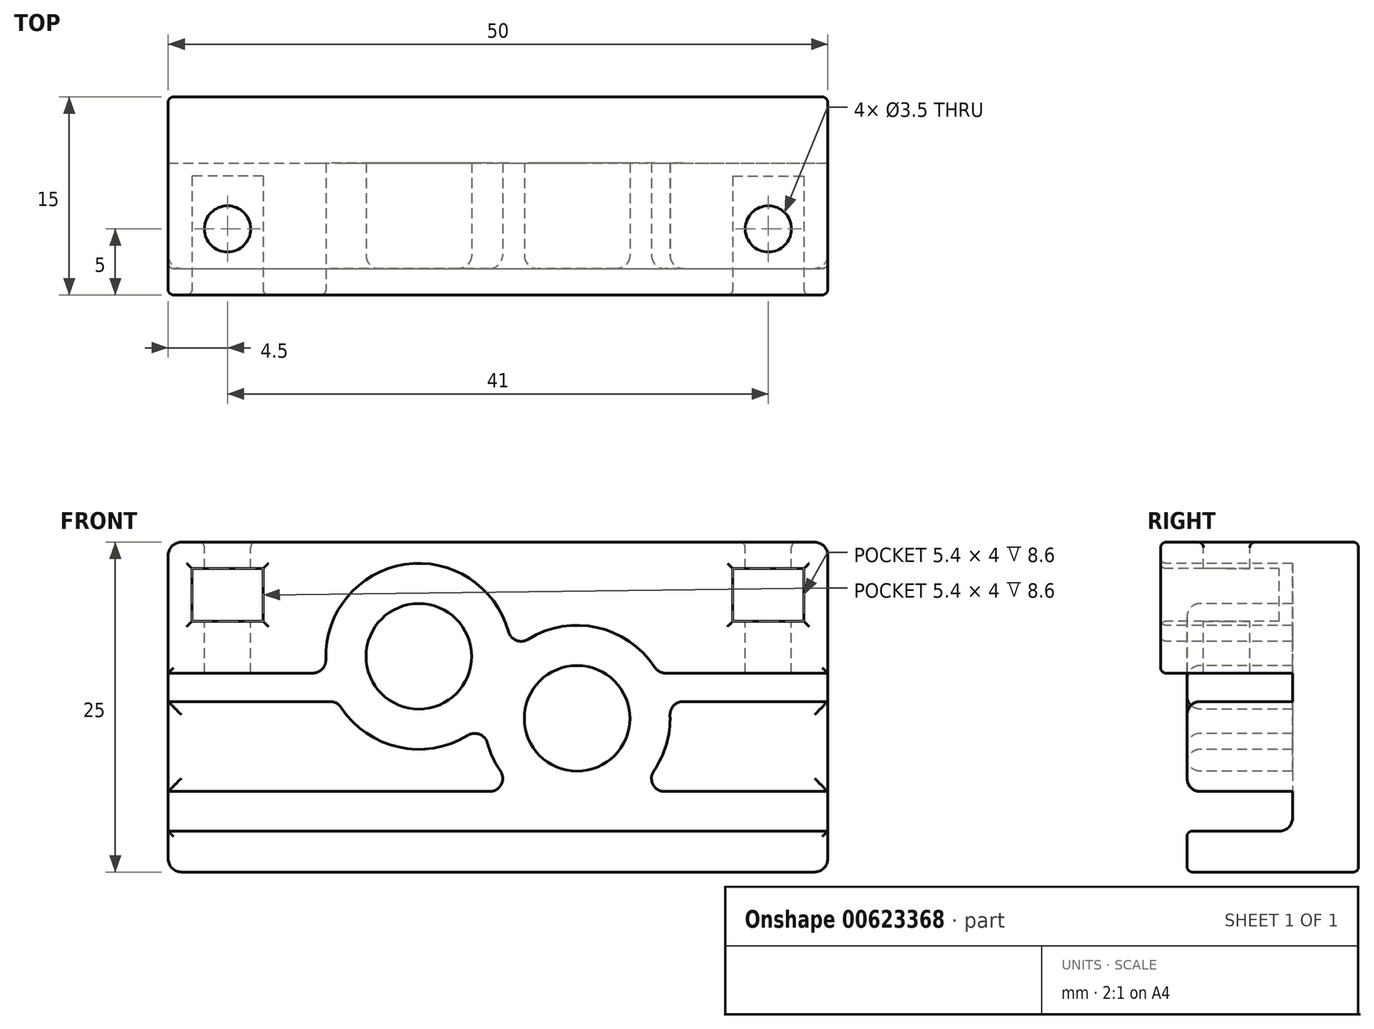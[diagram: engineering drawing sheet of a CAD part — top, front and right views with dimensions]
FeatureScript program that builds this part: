
annotation { "Feature Type Name" : "Feature", "Feature Type Description" : "" }
export const myFeature = defineFeature(function(context is Context, id is Id, definition is map)
    precondition{}
    {
        {
            var Q0;
            Q0=qCreatedBy(makeId("Top.planeOp"),FACE);
            var sketch = newSketch(context, id + "F0", { "sketchPlane" : qUnion([Q0])});
            skLineSegment(sketch, "E0.bottom", {"start": v(0, 0) * mm, "end": v(50, 0) * mm});
            skLineSegment(sketch, "E0.top", {"start": v(0, -20) * mm, "end": v(50, -20) * mm});
            skLineSegment(sketch, "E0.left", {"start": v(0, 0) * mm, "end": v(0, -20) * mm});
            skLineSegment(sketch, "E0.right", {"start": v(50, 0) * mm, "end": v(50, -20) * mm});
            skLineSegment(sketch, "E1", {"start": v(0, -10) * mm, "end": v(50, -10) * mm, "construction": true});
            skCircle(sketch, "E2", {"center": v(4.5, -10) * mm, "radius": 1.75 * mm});
            skCircle(sketch, "E3", {"center": v(45.5, -10) * mm, "radius": 1.75 * mm});
            skSolve(sketch);
        }
        {
            var Q0;
            Q0=makeQuery(id+"F0.imprint","IMPRINT",FACE,{"disambiguationData":[TD([[makeQuery(id+"F0.imprint","IMPRINT",EDGE,{"derivedFrom":sQuery(id+"F0.wireOp",EDGE,"E2")}),1.0]])]});
            var Q1;
            Q1=makeQuery(id+"F0.imprint","IMPRINT",FACE,{"disambiguationData":[TD([[makeQuery(id+"F0.imprint","IMPRINT",EDGE,{"derivedFrom":sQuery(id+"F0.wireOp",EDGE,"E3")}),1.0]])]});
            var Q2;
            Q2=makeQuery(id+"F0.imprint","IMPRINT",FACE,{"disambiguationData":[TD([[makeQuery(id+"F0.imprint","IMPRINT",EDGE,{"derivedFrom":sQuery(id+"F0.wireOp",EDGE,"E0.bottom")}),-1.0]])]});
            extrude(context, id + "F1", {"entities" : qUnion([Q0, Q1, Q2]), "depth" : 25 * mm, "offsetDistance" : 25 * mm});
        }
        {
            var Q0;
            Q0=makeQuery(id+"F1.opExtrude","SWEPT_FACE",FACE,{"disambiguationData":[OSD([sQuery(id+"F0.wireOp",EDGE,"E0.top")])]});
            var sketch = newSketch(context, id + "F2", { "sketchPlane" : qUnion([Q0])});
            skLineSegment(sketch, "E4", {"start": v(50, 14) * mm, "end": v(0, 14) * mm, "construction": true});
            skLineSegment(sketch, "E5", {"start": v(0, 18.7) * mm, "end": v(50, 18.7) * mm, "construction": true});
            skLineSegment(sketch, "E6.MirrorCS", {"start": v(0, 9.3) * mm, "end": v(50, 9.3) * mm, "construction": true});
            skLineSegment(sketch, "E7", {"start": v(25, 14) * mm, "end": v(25, 18.7) * mm, "construction": true});
            skLineSegment(sketch, "E8", {"start": v(25, 14) * mm, "end": v(25, 9.3) * mm, "construction": true});
            skCircle(sketch, "E9", {"center": v(31, 11.65) * mm, "radius": 4 * mm});
            skPoint(sketch, "E9.centerSnap0", {"position": v(25, 11.65) * mm});
            skCircle(sketch, "E10", {"center": v(19, 16.35) * mm, "radius": 4 * mm});
            skPoint(sketch, "E10.centerSnap0", {"position": v(25, 16.35) * mm});
            skLineSegment(sketch, "E11", {"start": v(0, 15.07) * mm, "end": v(12.07, 15.08) * mm});
            skLineSegment(sketch, "E12.MirrorCS", {"start": v(0, 12.92) * mm, "end": v(12.84, 12.93) * mm});
            skLineSegment(sketch, "E13", {"start": v(15.2, 15.08) * mm, "end": v(22.8, 15.08) * mm, "construction": true});
            skLineSegment(sketch, "E14", {"start": v(22.8, 15.08) * mm, "end": v(25.93, 15.08) * mm, "construction": true});
            skLineSegment(sketch, "E15", {"start": v(16.93, 12.93) * mm, "end": v(21.07, 12.93) * mm, "construction": true});
            skLineSegment(sketch, "E16", {"start": v(21.07, 12.93) * mm, "end": v(25.16, 12.93) * mm, "construction": true});
            skLineSegment(sketch, "E17", {"start": v(27.2, 12.93) * mm, "end": v(34.8, 12.93) * mm, "construction": true});
            skLineSegment(sketch, "E18", {"start": v(34.8, 12.93) * mm, "end": v(37.93, 12.93) * mm, "construction": true});
            skLineSegment(sketch, "E19", {"start": v(33.07, 15.08) * mm, "end": v(37.16, 15.08) * mm, "construction": true});
            skLineSegment(sketch, "E20", {"start": v(28.93, 15.08) * mm, "end": v(33.07, 15.08) * mm, "construction": true});
            skLineSegment(sketch, "E21", {"start": v(12.07, 15.08) * mm, "end": v(15.2, 15.08) * mm, "construction": true});
            skLineSegment(sketch, "E22", {"start": v(12.84, 12.93) * mm, "end": v(16.93, 12.93) * mm, "construction": true});
            skLineSegment(sketch, "E23", {"start": v(25.93, 15.08) * mm, "end": v(28.93, 15.08) * mm, "construction": true});
            skLineSegment(sketch, "E24", {"start": v(25.16, 12.93) * mm, "end": v(27.2, 12.93) * mm, "construction": true});
            skLineSegment(sketch, "E25", {"start": v(37.16, 15.08) * mm, "end": v(50, 15.08) * mm});
            skLineSegment(sketch, "E26", {"start": v(37.93, 12.93) * mm, "end": v(50, 12.93) * mm});
            skArc(sketch, "E27", {"start": v(12.84, 12.93) * mm, "mid": v(18, 9.37) * mm, "end": v(23.96, 11.34) * mm});
            skArc(sketch, "E28", {"start": v(12.07, 15.08) * mm, "mid": v(12.36, 13.97) * mm, "end": v(12.84, 12.93) * mm, "construction": true});
            skArc(sketch, "E29", {"start": v(26.04, 16.66) * mm, "mid": v(25.17, 19.76) * mm, "end": v(23, 22.15) * mm});
            skArc(sketch, "E30", {"start": v(23.96, 11.34) * mm, "mid": v(25.56, 13.78) * mm, "end": v(26.04, 16.66) * mm, "construction": true});
            skArc(sketch, "E31", {"start": v(37.16, 15.08) * mm, "mid": v(32, 18.63) * mm, "end": v(26.04, 16.66) * mm});
            skArc(sketch, "E32", {"start": v(37.93, 12.93) * mm, "mid": v(37.64, 14.03) * mm, "end": v(37.16, 15.08) * mm, "construction": true});
            skArc(sketch, "E33", {"start": v(26.04, 16.66) * mm, "mid": v(24.44, 14.22) * mm, "end": v(23.96, 11.34) * mm, "construction": true});
            skArc(sketch, "E34", {"start": v(23.96, 11.34) * mm, "mid": v(24.73, 8.42) * mm, "end": v(26.65, 6.1) * mm});
            skLineSegment(sketch, "E35", {"start": v(0, 4.6) * mm, "end": v(50, 4.6) * mm, "construction": true});
            skArc(sketch, "E36.0.startCap", {"start": v(0, 3.1) * mm, "mid": v(-1.5, 4.6) * mm, "end": v(0, 6.1) * mm});
            skArc(sketch, "E36.0.endCap", {"start": v(50, 6.1) * mm, "mid": v(51.5, 4.6) * mm, "end": v(50, 3.1) * mm});
            skLineSegment(sketch, "E36.0.left", {"start": v(0, 6.1) * mm, "end": v(50, 6.1) * mm});
            skLineSegment(sketch, "E36.0.right", {"start": v(0, 3.1) * mm, "end": v(50, 3.1) * mm});
            skArc(sketch, "E37", {"start": v(26.65, 6.1) * mm, "mid": v(31, 4.6) * mm, "end": v(35.35, 6.1) * mm, "construction": true});
            skArc(sketch, "E38", {"start": v(35.35, 6.1) * mm, "mid": v(37.6, 9.15) * mm, "end": v(37.93, 12.93) * mm});
            skArc(sketch, "E39", {"start": v(15, 22.15) * mm, "mid": v(12.49, 19.04) * mm, "end": v(12.07, 15.08) * mm});
            skArc(sketch, "E40", {"start": v(23, 22.15) * mm, "mid": v(19, 23.4) * mm, "end": v(15, 22.15) * mm});
            skPoint(sketch, "E41.0", {"position": v(0, 0) * mm});
            skLineSegment(sketch, "E42", {"start": v(38.27, 28.63) * mm, "end": v(42.23, 28.63) * mm, "construction": true});
            skLineSegment(sketch, "E43", {"start": v(38.27, 19.23) * mm, "end": v(42.97, 19.23) * mm, "construction": true});
            skLineSegment(sketch, "E44", {"start": v(38.57, 23.93) * mm, "end": v(43.39, 23.93) * mm, "construction": true});
            skSolve(sketch);
        }
        {
            var Q0;
            Q0=makeQuery(id+"F2.imprint","IMPRINT",FACE,{"disambiguationData":[TD([[makeQuery(id+"F2.imprint","IMPRINT",EDGE,{"derivedFrom":sQuery(id+"F2.wireOp",EDGE,"E9")}),-1.0]])]});
            var Q1;
            {var subQ0=sQuery(id+"F2.wireOp",EDGE,"E36.0.right");Q1=makeQuery(id+"F2.imprint","IMPRINT",FACE,{"disambiguationData":[TD([[makeQuery(id+"F2.imprint","IMPRINT",EDGE,{"derivedFrom":subQ0}),1.0]])]});}
            extrude(context, id + "F3", {"entities" : qUnion([Q0, Q1]), "operationType" : NewBodyOperationType.REMOVE, "oppositeDirection" : true, "depth" : 15 * mm, "offsetDistance" : 25 * mm});
        }
        {
            var Q0;
            Q0=makeQuery(id+"F2.imprint","IMPRINT",FACE,{"disambiguationData":[TD([[makeQuery(id+"F2.imprint","IMPRINT",EDGE,{"derivedFrom":sQuery(id+"F2.wireOp",EDGE,"E10")}),1.0]])]});
            var Q1;
            Q1=makeQuery(id+"F2.imprint","IMPRINT",FACE,{"disambiguationData":[TD([[makeQuery(id+"F2.imprint","IMPRINT",EDGE,{"derivedFrom":sQuery(id+"F2.wireOp",EDGE,"E9")}),1.0]])]});
            extrude(context, id + "F4", {"entities" : qUnion([Q0, Q1]), "operationType" : NewBodyOperationType.REMOVE, "oppositeDirection" : true, "depth" : 7 * mm, "offsetDistance" : 25 * mm});
        }
        {
            var Q0;
            {var subQ3=sQuery(id+"F0.wireOp",EDGE,"E0.top");Q0=makeQuery(id+"F3.boolean.opBoolean","SPLIT",FACE,{"disambiguationData":[TD([makeQuery(id+"F3.opExtrude","SWEPT_FACE",FACE,{"disambiguationData":[OSD([sQuery(id+"F2.wireOp",EDGE,"E12.MirrorCS")])]})])],"derivedFrom":makeQuery(id+"F1.opExtrude","SWEPT_FACE",FACE,{"disambiguationData":[OSD([subQ3])]})});}
            var Q1;
            {var subQ2=sQuery(id+"F0.wireOp",EDGE,"E0.top");Q1=makeQuery(id+"F3.boolean.opBoolean","SPLIT",FACE,{"disambiguationData":[TD([makeQuery(id+"F3.opExtrude","SWEPT_FACE",FACE,{"disambiguationData":[OSD([sQuery(id+"F2.wireOp",EDGE,"E26")])]})])],"derivedFrom":makeQuery(id+"F1.opExtrude","SWEPT_FACE",FACE,{"disambiguationData":[OSD([subQ2])]})});}
            var Q2;
            {var subQ2=sQuery(id+"F0.wireOp",EDGE,"E0.top");Q2=makeQuery(id+"F3.boolean.opBoolean","SPLIT",FACE,{"disambiguationData":[TD([makeQuery(id+"F3.opExtrude","SWEPT_FACE",FACE,{"disambiguationData":[OSD([sQuery(id+"F2.wireOp",EDGE,"E36.0.right")])]})])],"derivedFrom":makeQuery(id+"F1.opExtrude","SWEPT_FACE",FACE,{"disambiguationData":[OSD([subQ2])]})});}
            extrude(context, id + "F5", {"entities" : qUnion([Q0, Q1, Q2]), "operationType" : NewBodyOperationType.REMOVE, "oppositeDirection" : true, "depth" : 7 * mm, "offsetDistance" : 25 * mm});
        }
        {
            var Q0;
            {var subQ2=sQuery(id+"F0.wireOp",EDGE,"E0.top");Q0=makeQuery(id+"F3.boolean.opBoolean","SPLIT",FACE,{"disambiguationData":[TD([makeQuery(id+"F3.opExtrude","SWEPT_FACE",FACE,{"disambiguationData":[OSD([sQuery(id+"F2.wireOp",EDGE,"E11")])]})])],"derivedFrom":makeQuery(id+"F1.opExtrude","SWEPT_FACE",FACE,{"disambiguationData":[OSD([subQ2])]})});}
            extrude(context, id + "F6", {"entities" : qUnion([Q0]), "operationType" : NewBodyOperationType.REMOVE, "oppositeDirection" : true, "depth" : 5 * mm, "offsetDistance" : 25 * mm});
        }
        {
            var Q0;
            Q0=makeQuery(id+"F1.opExtrude","CAP_FACE",FACE,{"disambiguationData":[OSD([sQuery(id+"F0.wireOp",EDGE,"E0.bottom"),sQuery(id+"F0.wireOp",EDGE,"E0.top"),sQuery(id+"F0.wireOp",EDGE,"E0.left"),sQuery(id+"F0.wireOp",EDGE,"E0.right")])],"isStart":false});
            var sketch = newSketch(context, id + "F7", { "sketchPlane" : qUnion([Q0])});
            skCircle(sketch, "E45.0", {"center": v(4.5, -10) * mm, "radius": 1.75 * mm});
            skCircle(sketch, "E45.1", {"center": v(45.5, -10) * mm, "radius": 1.75 * mm});
            skSolve(sketch);
        }
        {
            var Q0;
            Q0=makeQuery(id+"F7.imprint","IMPRINT",FACE,{"disambiguationData":[TD([[makeQuery(id+"F7.imprint","IMPRINT",EDGE,{"derivedFrom":sQuery(id+"F7.wireOp",EDGE,"E45.0")}),1.0]])]});
            var Q1;
            Q1=makeQuery(id+"F7.imprint","IMPRINT",FACE,{"disambiguationData":[TD([[makeQuery(id+"F7.imprint","IMPRINT",EDGE,{"derivedFrom":sQuery(id+"F7.wireOp",EDGE,"E45.1")}),1.0]])]});
            var Q2;
            Q2=makeQuery(id+"F3.boolean.opBoolean","COPY",FACE,{"derivedFrom":makeQuery(id+"F3.opExtrude","SWEPT_FACE",FACE,{"disambiguationData":[OSD([sQuery(id+"F2.wireOp",EDGE,"E11")])]})});
            extrude(context, id + "F8", {"entities" : qUnion([Q0, Q1]), "operationType" : NewBodyOperationType.REMOVE, "endBound" : BoundingType.UP_TO_SURFACE, "oppositeDirection" : true, "depth" : 13.4 * mm, "endBoundEntityFace" : qUnion([Q2]), "offsetDistance" : 25 * mm});
        }
        {
            var Q0;
            Q0=makeQuery(id+"F6.boolean.opBoolean","COPY",FACE,{"derivedFrom":makeQuery(id+"F6.opExtrude","CAP_FACE",FACE,{"disambiguationData":[OSD([sQuery(id+"F0.wireOp",EDGE,"E0.top")])],"isStart":false})});
            var sketch = newSketch(context, id + "F9", { "sketchPlane" : qUnion([Q0])});
            skLineSegment(sketch, "E46.0", {"start": v(2.75, 25) * mm, "end": v(6.25, 25) * mm, "construction": true});
            skLineSegment(sketch, "E47.0", {"start": v(43.75, 25) * mm, "end": v(47.25, 25) * mm, "construction": true});
            skLineSegment(sketch, "E48.bottom", {"start": v(7.2, 19) * mm, "end": v(1.8, 19) * mm});
            skLineSegment(sketch, "E48.top", {"start": v(7.2, 23) * mm, "end": v(1.8, 23) * mm});
            skLineSegment(sketch, "E48.left", {"start": v(7.2, 19) * mm, "end": v(7.2, 23) * mm});
            skLineSegment(sketch, "E48.right", {"start": v(1.8, 19) * mm, "end": v(1.8, 23) * mm});
            skPoint(sketch, "E48.middle", {"position": v(4.5, 21) * mm});
            skPoint(sketch, "E48.middle.positionSnap0", {"position": v(4.5, 25) * mm});
            skPoint(sketch, "E48.centerSnap0", {"position": v(4.5, 25) * mm});
            skLineSegment(sketch, "E49", {"start": v(6.25, 25) * mm, "end": v(43.75, 25) * mm, "construction": true});
            skLineSegment(sketch, "E50", {"start": v(25, 25) * mm, "end": v(25, 18.94) * mm, "construction": true});
            skLineSegment(sketch, "E51.MirrorCS", {"start": v(42.8, 19) * mm, "end": v(48.2, 19) * mm});
            skLineSegment(sketch, "E52.MirrorCS", {"start": v(42.8, 19) * mm, "end": v(42.8, 23) * mm});
            skLineSegment(sketch, "E53.MirrorCS", {"start": v(48.2, 19) * mm, "end": v(48.2, 23) * mm});
            skLineSegment(sketch, "E54.MirrorCS", {"start": v(42.8, 23) * mm, "end": v(48.2, 23) * mm});
            skSolve(sketch);
        }
        {
            var Q0;
            Q0=makeQuery(id+"F9.imprint","IMPRINT",FACE,{"disambiguationData":[TD([[makeQuery(id+"F9.imprint","IMPRINT",EDGE,{"derivedFrom":sQuery(id+"F9.wireOp",EDGE,"E48.bottom")}),-1.0]])]});
            var Q1;
            Q1=makeQuery(id+"F9.imprint","IMPRINT",FACE,{"disambiguationData":[TD([[makeQuery(id+"F9.imprint","IMPRINT",EDGE,{"derivedFrom":sQuery(id+"F9.wireOp",EDGE,"E51.MirrorCS")}),1.0]])]});
            extrude(context, id + "F10", {"entities" : qUnion([Q0, Q1]), "operationType" : NewBodyOperationType.REMOVE, "oppositeDirection" : true, "depth" : 9 * mm, "offsetDistance" : 25 * mm});
        }
        {
            var Q0;
            Q0=makeQuery(id+"F4.boolean.opBoolean","COPY",FACE,{"derivedFrom":makeQuery(id+"F4.opExtrude","CAP_FACE",FACE,{"disambiguationData":[OSD([sQuery(id+"F2.wireOp",EDGE,"E10")])],"isStart":false})});
            var Q1;
            Q1=makeQuery(id+"F4.boolean.opBoolean","COPY",FACE,{"derivedFrom":makeQuery(id+"F4.opExtrude","CAP_FACE",FACE,{"disambiguationData":[OSD([sQuery(id+"F2.wireOp",EDGE,"E9")])],"isStart":false})});
            var Q2;
            {var subQ3=sQuery(id+"F0.wireOp",EDGE,"E0.top");Q2=makeQuery(id+"F5.boolean.opBoolean","COPY",FACE,{"derivedFrom":makeQuery(id+"F5.opExtrude","CAP_FACE",FACE,{"disambiguationData":[OSD([subQ3]),TDD([makeQuery(id+"F3.boolean.opBoolean","SPLIT",FACE,{"disambiguationData":[TD([makeQuery(id+"F3.opExtrude","SWEPT_FACE",FACE,{"disambiguationData":[OSD([sQuery(id+"F2.wireOp",EDGE,"E12.MirrorCS")])]})])],"derivedFrom":makeQuery(id+"F1.opExtrude","SWEPT_FACE",FACE,{"disambiguationData":[OSD([subQ3])]})})])],"isStart":false})});}
            var Q3;
            {var subQ2=sQuery(id+"F0.wireOp",EDGE,"E0.top");Q3=makeQuery(id+"F5.boolean.opBoolean","COPY",FACE,{"derivedFrom":makeQuery(id+"F5.opExtrude","CAP_FACE",FACE,{"disambiguationData":[OSD([subQ2]),TDD([makeQuery(id+"F3.boolean.opBoolean","SPLIT",FACE,{"disambiguationData":[TD([makeQuery(id+"F3.opExtrude","SWEPT_FACE",FACE,{"disambiguationData":[OSD([sQuery(id+"F2.wireOp",EDGE,"E26")])]})])],"derivedFrom":makeQuery(id+"F1.opExtrude","SWEPT_FACE",FACE,{"disambiguationData":[OSD([subQ2])]})})])],"isStart":false})});}
            var Q4;
            Q4=makeQuery(id+"F3.boolean.opBoolean","COPY",EDGE,{"derivedFrom":makeQuery(id+"F3.opExtrude","SWEPT_EDGE",EDGE,{"disambiguationData":[OSD([sQuery(id+"F2.wireOp",EDGE,"E26"),sQuery(id+"F2.wireOp",EDGE,"E38")])]})});
            var Q5;
            Q5=makeQuery(id+"F3.boolean.opBoolean","COPY",EDGE,{"derivedFrom":makeQuery(id+"F3.opExtrude","SWEPT_EDGE",EDGE,{"disambiguationData":[OSD([sQuery(id+"F2.wireOp",EDGE,"E36.0.left"),sQuery(id+"F2.wireOp",EDGE,"E38")])]})});
            var Q6;
            Q6=makeQuery(id+"F6.boolean.opBoolean","COPY",EDGE,{"derivedFrom":makeQuery(id+"F6.opExtrude","CAP_EDGE",EDGE,{"disambiguationData":[OSD([sQuery(id+"F2.wireOp",EDGE,"E29"),sQuery(id+"F2.wireOp",EDGE,"E39"),sQuery(id+"F2.wireOp",EDGE,"E40")])],"isStart":false})});
            var Q7;
            Q7=makeQuery(id+"F6.boolean.opBoolean","COPY",EDGE,{"derivedFrom":makeQuery(id+"F6.opExtrude","CAP_EDGE",EDGE,{"disambiguationData":[OSD([sQuery(id+"F2.wireOp",EDGE,"E31")])],"isStart":false})});
            var Q8;
            Q8=makeQuery(id+"F3.boolean.opBoolean","COPY",EDGE,{"derivedFrom":makeQuery(id+"F3.opExtrude","SWEPT_EDGE",EDGE,{"disambiguationData":[OSD([sQuery(id+"F2.wireOp",EDGE,"E29"),sQuery(id+"F2.wireOp",EDGE,"E31")])]})});
            var Q9;
            Q9=makeQuery(id+"F3.boolean.opBoolean","COPY",EDGE,{"derivedFrom":makeQuery(id+"F3.opExtrude","SWEPT_EDGE",EDGE,{"disambiguationData":[OSD([sQuery(id+"F2.wireOp",EDGE,"E25"),sQuery(id+"F2.wireOp",EDGE,"E31")])]})});
            var Q10;
            Q10=makeQuery(id+"F3.boolean.opBoolean","COPY",EDGE,{"derivedFrom":makeQuery(id+"F3.opExtrude","SWEPT_EDGE",EDGE,{"disambiguationData":[OSD([sQuery(id+"F2.wireOp",EDGE,"E11"),sQuery(id+"F2.wireOp",EDGE,"E39")])]})});
            var Q11;
            Q11=makeQuery(id+"F3.boolean.opBoolean","COPY",EDGE,{"derivedFrom":makeQuery(id+"F3.opExtrude","SWEPT_EDGE",EDGE,{"disambiguationData":[OSD([sQuery(id+"F0.wireOp",EDGE,"E0.top"),sQuery(id+"F0.wireOp",EDGE,"E0.left"),sQuery(id+"F2.wireOp",EDGE,"E36.0.startCap"),sQuery(id+"F2.wireOp",EDGE,"E36.0.left")])]})});
            var Q12;
            Q12=makeQuery(id+"F3.boolean.opBoolean","COPY",EDGE,{"derivedFrom":makeQuery(id+"F3.opExtrude","SWEPT_EDGE",EDGE,{"disambiguationData":[OSD([sQuery(id+"F0.wireOp",EDGE,"E0.top"),sQuery(id+"F0.wireOp",EDGE,"E0.left"),sQuery(id+"F2.wireOp",EDGE,"E12.MirrorCS")])]})});
            var Q13;
            Q13=makeQuery(id+"F3.boolean.opBoolean","COPY",EDGE,{"derivedFrom":makeQuery(id+"F3.opExtrude","SWEPT_EDGE",EDGE,{"disambiguationData":[OSD([sQuery(id+"F0.wireOp",EDGE,"E0.top"),sQuery(id+"F0.wireOp",EDGE,"E0.left"),sQuery(id+"F2.wireOp",EDGE,"E11")])]})});
            var Q14;
            Q14=makeQuery(id+"F3.boolean.opBoolean","COPY",EDGE,{"derivedFrom":makeQuery(id+"F3.opExtrude","SWEPT_EDGE",EDGE,{"disambiguationData":[OSD([sQuery(id+"F0.wireOp",EDGE,"E0.top"),sQuery(id+"F0.wireOp",EDGE,"E0.right"),sQuery(id+"F2.wireOp",EDGE,"E25")])]})});
            var Q15;
            Q15=makeQuery(id+"F3.boolean.opBoolean","COPY",EDGE,{"derivedFrom":makeQuery(id+"F3.opExtrude","SWEPT_EDGE",EDGE,{"disambiguationData":[OSD([sQuery(id+"F0.wireOp",EDGE,"E0.top"),sQuery(id+"F0.wireOp",EDGE,"E0.right"),sQuery(id+"F2.wireOp",EDGE,"E26")])]})});
            var Q16;
            Q16=makeQuery(id+"F3.boolean.opBoolean","COPY",EDGE,{"derivedFrom":makeQuery(id+"F3.opExtrude","SWEPT_EDGE",EDGE,{"disambiguationData":[OSD([sQuery(id+"F0.wireOp",EDGE,"E0.top"),sQuery(id+"F0.wireOp",EDGE,"E0.right"),sQuery(id+"F2.wireOp",EDGE,"E36.0.endCap"),sQuery(id+"F2.wireOp",EDGE,"E36.0.left")])]})});
            var Q17;
            Q17=makeQuery(id+"F3.boolean.opBoolean","COPY",EDGE,{"derivedFrom":makeQuery(id+"F3.opExtrude","SWEPT_EDGE",EDGE,{"disambiguationData":[OSD([sQuery(id+"F0.wireOp",EDGE,"E0.top"),sQuery(id+"F0.wireOp",EDGE,"E0.right"),sQuery(id+"F2.wireOp",EDGE,"E36.0.endCap"),sQuery(id+"F2.wireOp",EDGE,"E36.0.right")])]})});
            var Q18;
            Q18=makeQuery(id+"F3.boolean.opBoolean","COPY",EDGE,{"derivedFrom":makeQuery(id+"F3.opExtrude","CAP_EDGE",EDGE,{"disambiguationData":[OSD([sQuery(id+"F2.wireOp",EDGE,"E36.0.right")])],"isStart":false})});
            var Q19;
            Q19=makeQuery(id+"F3.boolean.opBoolean","COPY",EDGE,{"derivedFrom":makeQuery(id+"F3.opExtrude","SWEPT_EDGE",EDGE,{"disambiguationData":[OSD([sQuery(id+"F2.wireOp",EDGE,"E34"),sQuery(id+"F2.wireOp",EDGE,"E36.0.left")])]})});
            var Q20;
            Q20=makeQuery(id+"F3.boolean.opBoolean","COPY",EDGE,{"derivedFrom":makeQuery(id+"F3.opExtrude","SWEPT_EDGE",EDGE,{"disambiguationData":[OSD([sQuery(id+"F2.wireOp",EDGE,"E27"),sQuery(id+"F2.wireOp",EDGE,"E34")])]})});
            var Q21;
            Q21=makeQuery(id+"F3.boolean.opBoolean","COPY",EDGE,{"derivedFrom":makeQuery(id+"F3.opExtrude","SWEPT_EDGE",EDGE,{"disambiguationData":[OSD([sQuery(id+"F2.wireOp",EDGE,"E12.MirrorCS"),sQuery(id+"F2.wireOp",EDGE,"E27")])]})});
            var Q22;
            Q22=makeQuery(id+"F1.opExtrude","CAP_EDGE",EDGE,{"disambiguationData":[OSD([sQuery(id+"F0.wireOp",EDGE,"E0.left")])],"isStart":true});
            var Q23;
            Q23=makeQuery(id+"F1.opExtrude","CAP_EDGE",EDGE,{"disambiguationData":[OSD([sQuery(id+"F0.wireOp",EDGE,"E0.right")])],"isStart":true});
            var Q24;
            Q24=makeQuery(id+"F1.opExtrude","CAP_EDGE",EDGE,{"disambiguationData":[OSD([sQuery(id+"F0.wireOp",EDGE,"E0.right")])],"isStart":false});
            var Q25;
            Q25=makeQuery(id+"F1.opExtrude","CAP_EDGE",EDGE,{"disambiguationData":[OSD([sQuery(id+"F0.wireOp",EDGE,"E0.left")])],"isStart":false});
            var Q26;
            Q26=makeQuery(id+"F6.boolean.opBoolean","COPY",EDGE,{"derivedFrom":makeQuery(id+"F6.opExtrude","CAP_EDGE",EDGE,{"disambiguationData":[OSD([sQuery(id+"F2.wireOp",EDGE,"E25")])],"isStart":false})});
            var Q27;
            Q27=makeQuery(id+"F6.boolean.opBoolean","COPY",EDGE,{"derivedFrom":makeQuery(id+"F6.opExtrude","CAP_EDGE",EDGE,{"disambiguationData":[OSD([sQuery(id+"F2.wireOp",EDGE,"E11")])],"isStart":false})});
            var Q28;
            Q28=makeQuery(id+"F3.boolean.opBoolean","COPY",EDGE,{"derivedFrom":makeQuery(id+"F3.opExtrude","SWEPT_EDGE",EDGE,{"disambiguationData":[OSD([sQuery(id+"F0.wireOp",EDGE,"E0.top"),sQuery(id+"F0.wireOp",EDGE,"E0.left"),sQuery(id+"F2.wireOp",EDGE,"E36.0.startCap"),sQuery(id+"F2.wireOp",EDGE,"E36.0.right")])]})});
            var Q29;
            {var subQ0=sQuery(id+"F0.wireOp",EDGE,"E0.left");var subQ1=sQuery(id+"F0.wireOp",EDGE,"E0.top");var subQ2=makeQuery(id+"F1.opExtrude","SWEPT_EDGE",EDGE,{"disambiguationData":[OSD([subQ1,subQ0])]});Q29=makeQuery(id+"F3.boolean.opBoolean","COPY",EDGE,{"derivedFrom":makeQuery(id+"F3.opExtrude","CAP_EDGE",EDGE,{"disambiguationData":[OSD([subQ1,subQ0]),TDD([makeQuery(id+"F2.imprint","IMPRINT",EDGE,{"disambiguationData":[TD([[makeQuery(id+"F2.imprint","INTERSECT",VERTEX,{"derivedFrom":[subQ2,sQuery(id+"F2.wireOp",EDGE,"E11")]}),-1.0]])],"derivedFrom":subQ2})])],"isStart":false})});}
            var Q30;
            {var subQ0=sQuery(id+"F0.wireOp",EDGE,"E0.right");var subQ1=sQuery(id+"F0.wireOp",EDGE,"E0.top");var subQ2=makeQuery(id+"F1.opExtrude","SWEPT_EDGE",EDGE,{"disambiguationData":[OSD([subQ1,subQ0])]});Q30=makeQuery(id+"F3.boolean.opBoolean","COPY",EDGE,{"derivedFrom":makeQuery(id+"F3.opExtrude","CAP_EDGE",EDGE,{"disambiguationData":[OSD([subQ1,subQ0]),TDD([makeQuery(id+"F2.imprint","IMPRINT",EDGE,{"disambiguationData":[TD([[makeQuery(id+"F2.imprint","INTERSECT",VERTEX,{"derivedFrom":[subQ2,sQuery(id+"F2.wireOp",EDGE,"E25")]}),-1.0]])],"derivedFrom":subQ2})])],"isStart":false})});}
            fillet(context, id + "F11", {"entities" : qUnion([Q0, Q1, Q2, Q3, Q4, Q5, Q6, Q7, Q8, Q9, Q10, Q11, Q12, Q13, Q14, Q15, Q16, Q17, Q18, Q19, Q20, Q21, Q22, Q23, Q24, Q25, Q26, Q27, Q28, Q29, Q30]), "radius" : 1 * mm, "tangentPropagation" : true, "allowEdgeOverflow" : false});
        }
        {
            var Q0;
            Q0=makeQuery(id+"F1.opExtrude","SWEPT_FACE",FACE,{"disambiguationData":[OSD([sQuery(id+"F0.wireOp",EDGE,"E0.bottom")])]});
            var Q1;
            Q1=makeQuery(id+"F1.opExtrude","CAP_FACE",FACE,{"disambiguationData":[OSD([sQuery(id+"F0.wireOp",EDGE,"E0.bottom"),sQuery(id+"F0.wireOp",EDGE,"E0.top"),sQuery(id+"F0.wireOp",EDGE,"E0.left"),sQuery(id+"F0.wireOp",EDGE,"E0.right")])],"isStart":false});
            var Q2;
            Q2=makeQuery(id+"F6.boolean.opBoolean","COPY",FACE,{"derivedFrom":makeQuery(id+"F6.opExtrude","CAP_FACE",FACE,{"disambiguationData":[OSD([sQuery(id+"F0.wireOp",EDGE,"E0.top")])],"isStart":false})});
            var Q3;
            {var subQ2=sQuery(id+"F0.wireOp",EDGE,"E0.top");Q3=makeQuery(id+"F5.boolean.opBoolean","COPY",FACE,{"derivedFrom":makeQuery(id+"F5.opExtrude","CAP_FACE",FACE,{"disambiguationData":[OSD([subQ2]),TDD([makeQuery(id+"F3.boolean.opBoolean","SPLIT",FACE,{"disambiguationData":[TD([makeQuery(id+"F3.opExtrude","SWEPT_FACE",FACE,{"disambiguationData":[OSD([sQuery(id+"F2.wireOp",EDGE,"E36.0.right")])]})])],"derivedFrom":makeQuery(id+"F1.opExtrude","SWEPT_FACE",FACE,{"disambiguationData":[OSD([subQ2])]})})])],"isStart":false})});}
            fillet(context, id + "F12", {"entities" : qUnion([Q0, Q1, Q2, Q3]), "radius" : 0.4 * mm, "tangentPropagation" : true, "allowEdgeOverflow" : false});
        }
    });
